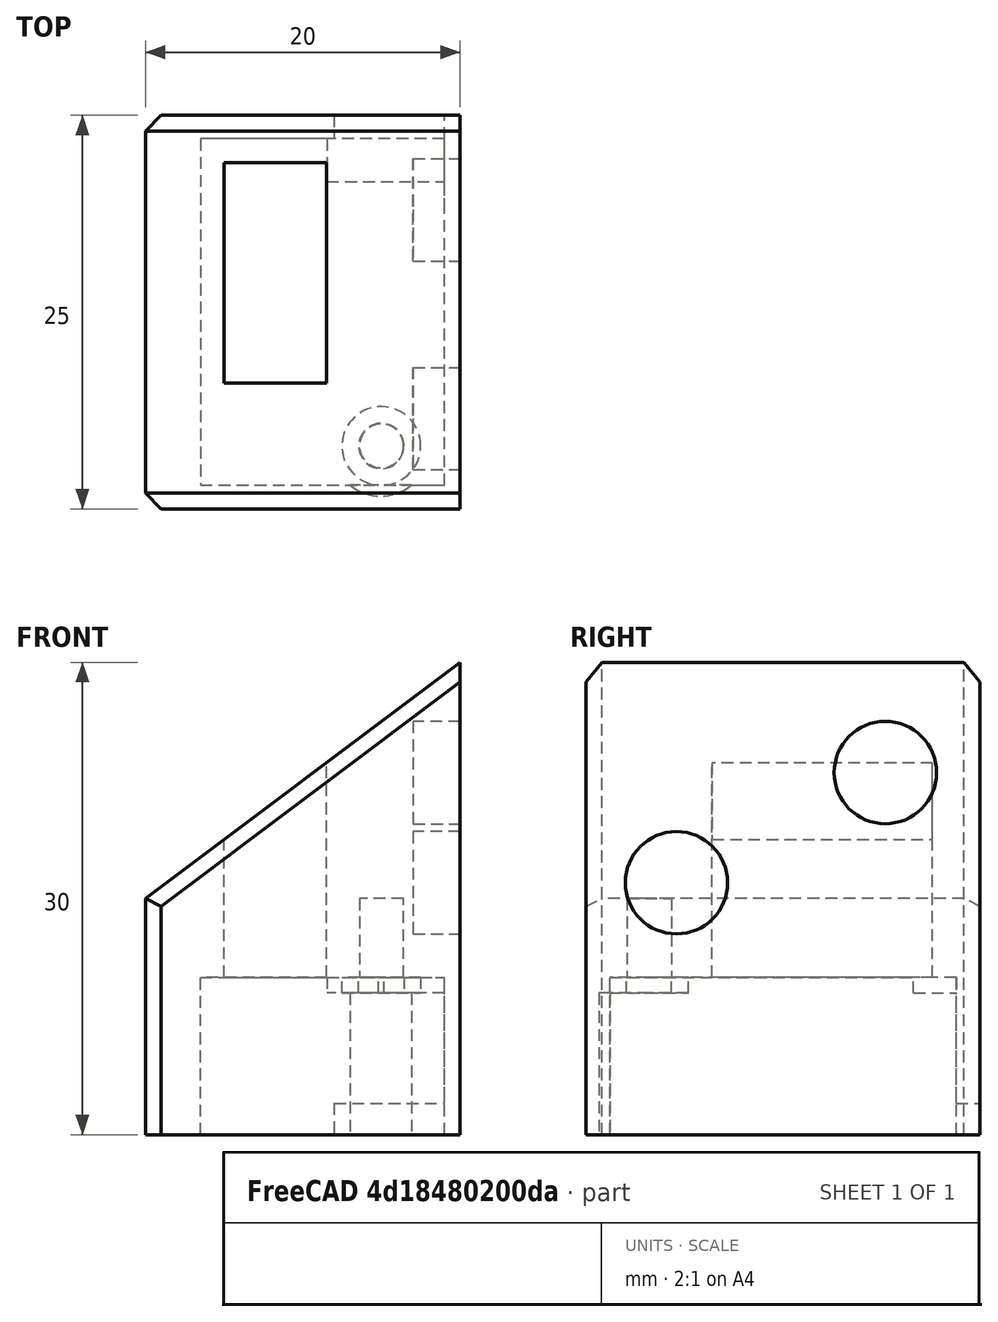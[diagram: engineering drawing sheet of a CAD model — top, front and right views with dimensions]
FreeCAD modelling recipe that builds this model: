
FCSTD DOCUMENT  (FreeCAD 0.19R)
Label: ZswitchHolder
License: All rights reserved
LicenseURL: http://en.wikipedia.org/wiki/All_rights_reserved
objects: Sketcher::SketchObject×8, PartDesign::Pocket×6, PartDesign::Pad×2, PartDesign::Chamfer×1, PartDesign::Body×1, Mesh::Feature×1
note: 27 computed .brp shape members not serialized (recipe doc carries the construction recipe); baked Part::Feature solids carry a one-line shape summary decoded from their .brp

FEATURE [Sketcher::SketchObject] Sketch
  FullyConstrained = true
  MapMode = 5
  Placement = pos=(0,0,0) rot=(1,0,0;1.5708rad)
  Support = -> [XZ_Plane]
  sketch-geometry (4):
    g0: LineSegment StartX=0 StartY=0 StartZ=0 EndX=-20 EndY=0 EndZ=0
    g1: LineSegment StartX=-20 StartY=0 StartZ=0 EndX=-20 EndY=15 EndZ=0
    g2: LineSegment StartX=-20 StartY=15 StartZ=0 EndX=0 EndY=30 EndZ=0
    g3: LineSegment StartX=0 StartY=30 StartZ=0 EndX=0 EndY=0 EndZ=0
  constraints (11):
    c: Coincident(g-1,g0)
    c: PointOnObject(g0,g-1)
    c: Coincident(g0,g1)
    c: Vertical(g1)
    c: Coincident(g1,g2)
    c: PointOnObject(g2,g-2)
    c: Coincident(g2,g3)
    c: Coincident(g3,g0)
    c: Distance(g0) = 20
    c: Distance(g1) = 15
    c: Distance(g3) = 30
FEATURE [PartDesign::Pad] Pad
  Direction = (1,1,1)
  Length = 25
  Length2 = 100
  Placement = pos=(0,0,0) rot=(1,0,0;1.5708rad)
  Profile = -> Sketch
  Type = 0
FEATURE [Sketcher::SketchObject] Sketch001
  FullyConstrained = true
  MapMode = 5
  Placement = pos=(0,0,0) rot=(1,0,0;3.14159rad)
  Support = -> [Pad]
  sketch-geometry (4):
    g0: LineSegment StartX=-16.5 StartY=23.5 StartZ=0 EndX=-1 EndY=23.5 EndZ=0
    g1: LineSegment StartX=-1 StartY=23.5 StartZ=0 EndX=-1 EndY=1.5 EndZ=0
    g2: LineSegment StartX=-1 StartY=1.5 StartZ=0 EndX=-16.5 EndY=1.5 EndZ=0
    g3: LineSegment StartX=-16.5 StartY=1.5 StartZ=0 EndX=-16.5 EndY=23.5 EndZ=0
  constraints (12):
    c: Coincident(g0,g1)
    c: Coincident(g1,g2)
    c: Coincident(g2,g3)
    c: Coincident(g3,g0)
    c: Horizontal(g0)
    c: Horizontal(g2)
    c: Vertical(g1)
    c: Vertical(g3)
    c: DistanceX(g0) = -1
    c: Distance(g0) = 15.5
    c: DistanceY(g1) = 1.5
    c: Distance(g1) = 22
FEATURE [PartDesign::Pocket] Pocket
  BaseFeature = -> Pad
  Length = 10
  Length2 = 100
  Placement = pos=(0,0,0) rot=(1,0,0;1.5708rad)
  Profile = -> Sketch001
  Type = 0
FEATURE [Sketcher::SketchObject] Sketch002
  FullyConstrained = false
  MapMode = 5
  Placement = pos=(0,8.9e-15,10) rot=(1,0,0;3.14159rad)
  Support = -> [Pocket]
  sketch-geometry (3):
    g0: Circle CenterX=-5 CenterY=21 CenterZ=0 NormalX=0 NormalY=0 NormalZ=1 AngleXU=0 Radius=1.4
    g1: Circle CenterX=-5 CenterY=1 CenterZ=0 NormalX=0 NormalY=0 NormalZ=1 AngleXU=0 Radius=1.4
    g2: LineSegment StartX=-32.0421 StartY=11 StartZ=0 EndX=23.524 EndY=11 EndZ=0
  constraints (7):
    c: Diameter(g1) = 2.8
    c: Equal(g1,g0)
    c: Distance(g1,g0) = 20
    c: DistanceX(g1) = -5
    c: DistanceX(g0,g1) = 0
    c: Symmetric(g1,g0,g2)
    c: DistanceY(g2) = 11
FEATURE [PartDesign::Pocket] Pocket001
  BaseFeature = -> Pocket
  Length = 5
  Length2 = 100
  Placement = pos=(0,0,0) rot=(1,0,0;1.5708rad)
  Profile = -> Sketch002
  Type = 0
FEATURE [Sketcher::SketchObject] Sketch003
  FullyConstrained = false
  MapMode = 5
  Placement = pos=(0,8.9e-15,10) rot=(1,0,0;3.14159rad)
  Support = -> [Pocket001]
  sketch-geometry (5):
    g0: LineSegment StartX=-33.3628 StartY=10 StartZ=0 EndX=27.1042 EndY=10 EndZ=0
    g1: LineSegment StartX=-15 StartY=17 StartZ=0 EndX=-8.5 EndY=17 EndZ=0
    g2: LineSegment StartX=-8.5 StartY=17 StartZ=0 EndX=-8.5 EndY=3 EndZ=0
    g3: LineSegment StartX=-8.5 StartY=3 StartZ=0 EndX=-15 EndY=3 EndZ=0
    g4: LineSegment StartX=-15 StartY=3 StartZ=0 EndX=-15 EndY=17 EndZ=0
  constraints (13):
    c: Horizontal(g0)
    c: DistanceY(g0) = 10
    c: Coincident(g1,g2)
    c: Coincident(g2,g3)
    c: Coincident(g3,g4)
    c: Coincident(g4,g1)
    c: Horizontal(g1)
    c: Horizontal(g3)
    c: Vertical(g2)
    c: Symmetric(g3,g1,g0)
    c: Distance(g1) = 6.5
    c: DistanceX(g3) = -15
    c: Distance(g2) = 14
FEATURE [PartDesign::Pocket] Pocket002
  BaseFeature = -> Pocket001
  Length = 20
  Length2 = 100
  Placement = pos=(0,0,0) rot=(1,0,0;1.5708rad)
  Profile = -> Sketch003
  Type = 0
FEATURE [Sketcher::SketchObject] Sketch004
  FullyConstrained = true
  MapMode = 5
  Placement = pos=(0,0,0) rot=(0.707107,0,0.707107;3.14159rad)
  Support = -> [Pocket002]
  sketch-geometry (2):
    g0: Circle CenterX=16 CenterY=19.2665 CenterZ=0 NormalX=0 NormalY=0 NormalZ=1 AngleXU=0 Radius=3.25
    g1: Circle CenterX=23 CenterY=6 CenterZ=0 NormalX=0 NormalY=0 NormalZ=1 AngleXU=0 Radius=3.25
  constraints (6):
    c: Diameter(g1) = 6.5
    c: Equal(g1,g0)
    c: Distance(g1,g0) = 15
    c: DistanceX(g1) = 23
    c: DistanceX(g0) = 16
    c: DistanceY(g1) = 6
FEATURE [PartDesign::Pocket] Pocket003
  BaseFeature = -> Pocket002
  Length = 3
  Length2 = 100
  Placement = pos=(0,0,0) rot=(1,0,0;1.5708rad)
  Profile = -> Sketch004
  Type = 0
FEATURE [Sketcher::SketchObject] Sketch005
  FullyConstrained = false
  MapMode = 5
  Placement = pos=(0,0,0) rot=(1,0,0;3.14159rad)
  sketch-geometry (4):
    g0: LineSegment StartX=-8 StartY=6.00509 StartZ=0 EndX=-1 EndY=6.00509 EndZ=0
    g1: LineSegment StartX=-1 StartY=6.00509 StartZ=0 EndX=-1 EndY=-4.64862 EndZ=0
    g2: LineSegment StartX=-1 StartY=-4.64862 StartZ=0 EndX=-8 EndY=-4.64862 EndZ=0
    g3: LineSegment StartX=-8 StartY=-4.64862 StartZ=0 EndX=-8 EndY=6.00509 EndZ=0
  constraints (10):
    c: Coincident(g0,g1)
    c: Coincident(g1,g2)
    c: Coincident(g2,g3)
    c: Coincident(g3,g0)
    c: Horizontal(g0)
    c: Horizontal(g2)
    c: Vertical(g1)
    c: Vertical(g3)
    c: DistanceX(g1) = -1
    c: Distance(g0) = 7
FEATURE [Sketcher::SketchObject] Sketch006
  FullyConstrained = false
  MapMode = 5
  Placement = pos=(0,2.9e-14,10) rot=(1,0,0;3.14159rad)
  sketch-geometry (6):
    g0: Circle CenterX=-5.01275 CenterY=21.0064 CenterZ=0 NormalX=0 NormalY=0 NormalZ=1 AngleXU=0 Radius=2.5
    g1: Circle CenterX=-5.01275 CenterY=21.0064 CenterZ=0 NormalX=0 NormalY=0 NormalZ=1 AngleXU=0 Radius=1.43758
    g2: LineSegment StartX=-8.47 StartY=4.20523 StartZ=0 EndX=-0.840312 EndY=4.20523 EndZ=0
    g3: LineSegment StartX=-0.840312 StartY=4.20523 StartZ=0 EndX=-0.840312 EndY=1.3763 EndZ=0
    g4: LineSegment StartX=-0.840312 StartY=1.3763 StartZ=0 EndX=-8.47 EndY=1.3763 EndZ=0
    g5: LineSegment StartX=-8.47 StartY=1.3763 StartZ=0 EndX=-8.47 EndY=4.20523 EndZ=0
  constraints (11):
    c: Diameter(g0) = 5
    c: Coincident(g1,g0)
    c: Coincident(g2,g3)
    c: Coincident(g3,g4)
    c: Coincident(g4,g5)
    c: Coincident(g5,g2)
    c: Horizontal(g2)
    c: Horizontal(g4)
    c: Vertical(g3)
    c: Vertical(g5)
    c: DistanceX(g2) = -8.47
FEATURE [Sketcher::SketchObject] Sketch007
  FullyConstrained = false
  MapMode = 5
  Placement = pos=(0,0,0) rot=(1,0,0;3.14159rad)
  sketch-geometry (1):
    g0: Circle CenterX=-5.05509 CenterY=21.0517 CenterZ=0 NormalX=0 NormalY=0 NormalZ=1 AngleXU=0 Radius=3.1314
FEATURE [PartDesign::Chamfer] Chamfer
  Angle = 45
  Base = -> Pocket003 [Edge16,Edge17,Edge14,Edge15]
  BaseFeature = -> Pocket003
  ChamferType = 0
  FlipDirection = false
  Placement = pos=(0,0,0) rot=(1,0,0;1.5708rad)
  Size = 1
  Size2 = 1
  SupportTransform = false
FEATURE [PartDesign::Pocket] Pocket004
  BaseFeature = -> Chamfer
  Length = 2
  Length2 = 100
  Placement = pos=(0,0,0) rot=(1,0,0;1.5708rad)
  Profile = -> Sketch005
  Type = 0
FEATURE [PartDesign::Pad] Pad001
  BaseFeature = -> Pocket004
  Direction = (1,1,1)
  Length = 1
  Length2 = 100
  Placement = pos=(0,0,0) rot=(1,0,0;1.5708rad)
  Profile = -> Sketch006
  Type = 0
FEATURE [PartDesign::Pocket] Pocket005
  BaseFeature = -> Pad001
  Length = 9
  Length2 = 100
  Placement = pos=(0,0,0) rot=(1,0,0;1.5708rad)
  Profile = -> Sketch007
  Type = 0
FEATURE [PartDesign::Body] Body
  Group = -> [Sketch,Pad,Sketch001,Pocket,Sketch002,Pocket001,Sketch003,Pocket002,Sketch004,Pocket003,Sketch005,Sketch006,Sketch007,Chamfer,Pocket004,Pad001,Pocket005]
  Origin = -> Origin
  Tip = -> Pocket005
FEATURE [Mesh::Feature] Mesh  label="Pocket005 (Meshed)"
